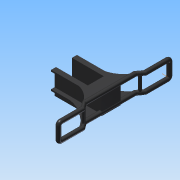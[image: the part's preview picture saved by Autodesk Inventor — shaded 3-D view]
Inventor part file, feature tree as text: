
AUTODESK INVENTOR PART (.ipt)
format: ipt  version: 2014 (Build 180170000, 170)  size: 480,256 bytes
history: native  units: in
note: dims shown in document units (in); Inventor stores cm internally (conversion verified against a paired STEP export)
features: sketch x19, extrude x15, plane x6, other x6, mirror x4, revolve x2, loft x1, pattern_linear x1, fillet x1, chamfer x1, projected_geometry x1
ambient origin geometry x8: Origin, YZ Plane, XZ Plane, XY Plane, X Axis, Y Axis, Z Axis, Center Point
bodies: Solid1 (feature_tree)
feature tree (57):
  extrude  "Extrusion1"  Depth=1.3in
  extrude  "Extrusion2"  Depth=0.1in
  extrude  "Extrusion3"  Depth=0.1in
  extrude  "Extrusion4"  Depth=0.46in
  sketch  "Sketch7"  dims[d11=1.18in d12=0.0in d13=1.1in]
  plane  "Work Plane4"
  sketch  "Sketch10"  dims[d14=0.1in d15=0.0in d22=0.3in]
  plane  "Work Plane7"
  plane  "Work Plane8"
  sketch  "Sketch13"  dims[d23=0.05in d29=1.15in]
  plane  "Work Plane9"
  sketch  "Sketch14"  dims[d36=0.4in d37=0.6in]
  extrude  "Extrusion6"  Depth=1.18in
  extrude  "Extrusion7"  Depth=0.3in
  loft  "Loft1"
  mirror  "Mirror1"
  extrude  "Extrusion8"  Depth=0.6in
  pattern_linear  "Rectangular Pattern1"  Count1=2 Spacing1=1.18in
  extrude  "Extrusion9"  Depth=1.342in
  fillet  "Fillet1"  Radius=0.2in
  extrude  "Extrusion10"  Depth=1.342in TaperAngle=0.0deg
  extrude  "Extrusion11"  Depth=1.342in TaperAngle=0.0deg
  mirror  "Mirror2"
  plane  "Work Plane10"
  sketch  "Sketch20"  dims[d46=0.0in d47=90.0deg]
  plane  "Work Plane11"
  extrude  "Extrusion12"  TaperAngle=90.0deg  [1 undecoded]
  other  "Work Axis4"
  revolve  "Revolution1"  [1 undecoded]
  other  "Work Axis5"
  revolve  "Revolution2"  [1 undecoded]
  mirror  "Mirror3"
  extrude  "Extrusion13"  Depth=0.1in TaperAngle=0.0deg
  extrude  "Extrusion14"  Depth=0.436in
  extrude  "Extrusion15"  Depth=0.436in
  mirror  "Mirror4"
  extrude  "Extrusion16"  Depth=0.1in TaperAngle=0.0deg
  chamfer  "Chamfer1"  Distance=0.436in
  sketch  "Sketch1"  dims[d0=1.342in d2=1.3in]
  sketch  "Sketch2"  dims[d3=3.38in d4=0.0in d5=0.1in]
  sketch  "Sketch3"  dims[d6=0.1in d7=0.1in]
  sketch  "Sketch4"  dims[d8=1.18in d9=0.0in d10=0.46in]
  other  "Edges1"
  other  "Edges2"
  sketch  "Sketch15"  dims[d39=1.6in]
  sketch  "Sketch17"  dims[d40=1.15in d41=0.0in]
  sketch  "Sketch18"  dims[d42=1.15in d43=0.0in]
  sketch  "Sketch19"  dims[d44=0.0in d45=90.0deg]
  sketch  "Sketch21"  dims[d48=1.15in d49=0.0in d50=0.7874in d52=1.18in]
  sketch  "Sketch23"  dims[d53=1.342in d54=0.0in d55=0.0625in d56=0.2in]
  other  "Work Axis6"
  other  "Work Axis7"
  sketch  "Sketch24"  dims[d59=1.342in d60=0.0in d61=1.342in d62=0.0in]
  sketch  "Sketch25"  dims[d63=0.3in d64=1.342in d65=0.0in]
  sketch  "Sketch26"  dims[d66=90.0deg d67=90.0deg]
  sketch  "Sketch27"  dims[d68=2.0in d70=0.26in d71=0.1in d72=0.0in d73=0.1in d74=0.0in d75=1.4in d76=0.15in d77=0.1in d78=0.0in d79=0.436in d80=0.0in d81=0.375in d82=0.125in d83=45.0deg]
  projected_geometry  "Project Cut Edges1"
note: 3 required parameter values undecoded (feature->parameter linkage not recoverable at this tier; creation-order binding heuristic only, values carry confidence <= 0.55)